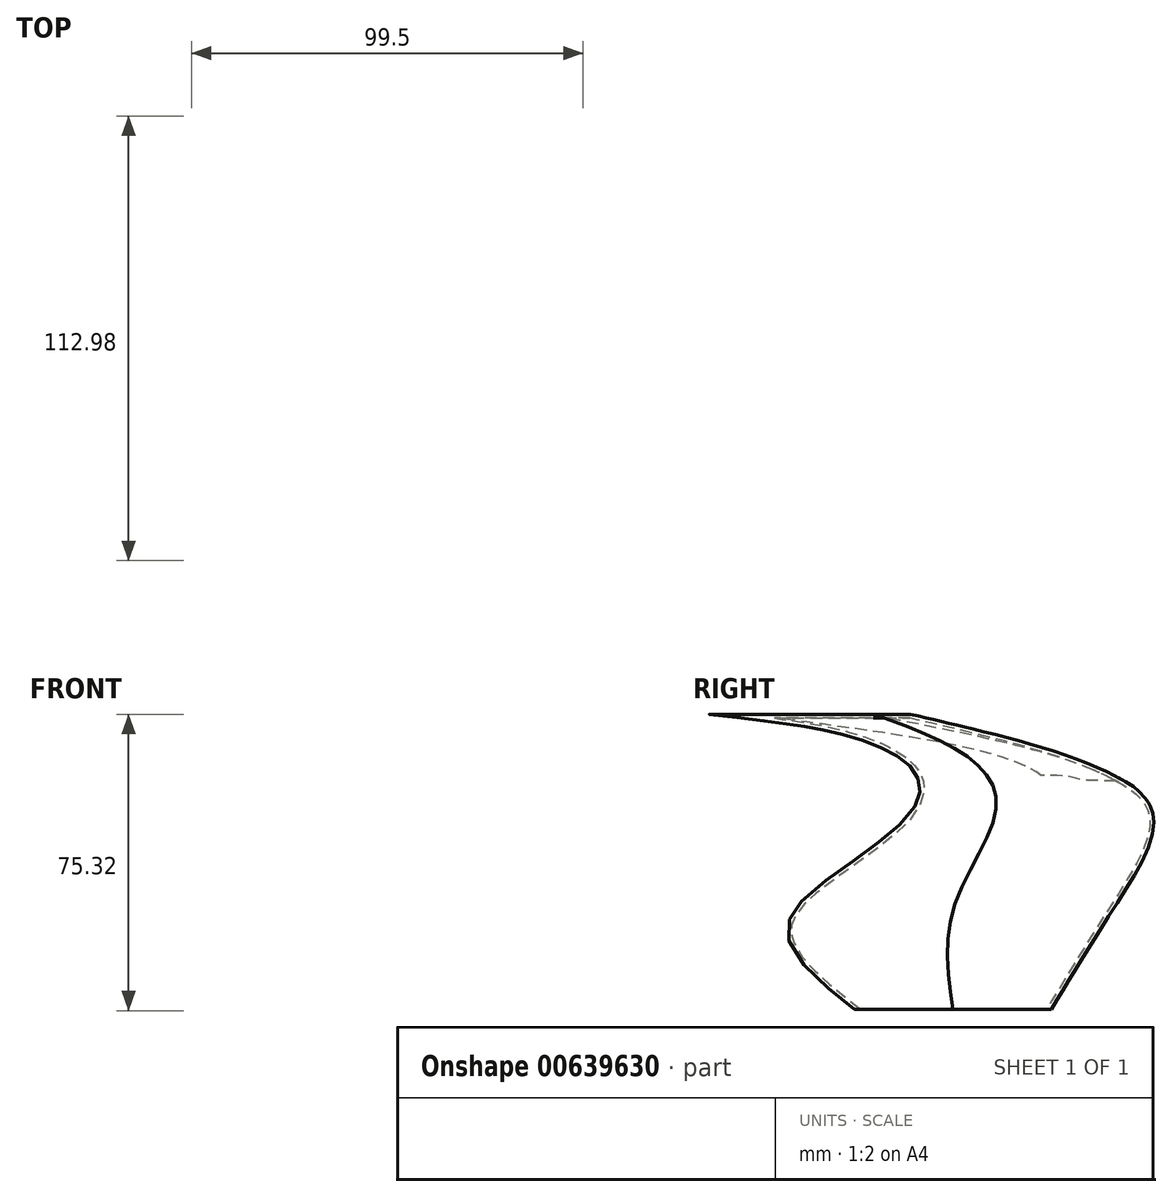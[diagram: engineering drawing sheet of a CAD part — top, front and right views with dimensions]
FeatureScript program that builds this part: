
annotation { "Feature Type Name" : "Feature", "Feature Type Description" : "" }
export const myFeature = defineFeature(function(context is Context, id is Id, definition is map)
    precondition{}
    {
        {
            var Q0;
            Q0=qCreatedBy(makeId("Top.planeOp"),FACE);
            var sketch = newSketch(context, id + "F0", { "sketchPlane" : qUnion([Q0])});
            skCircle(sketch, "E0", {"center": v(0, 0) * mm, "radius": 25 * mm});
            skSolve(sketch);
        }
        {
            var Q0;
            Q0=qCreatedBy(makeId("Top.planeOp"),FACE);
            cPlane(context, id + "F1", {"entities" : qUnion([Q0]), "cplaneType" : CPlaneType.OFFSET, "offset" : 25 * mm, "width" : 150 * mm, "height" : 150 * mm});
        }
        {
            var Q0;
            Q0=qCreatedBy(id+"F1.planeOp",FACE);
            cPlane(context, id + "F2", {"entities" : qUnion([Q0]), "cplaneType" : CPlaneType.OFFSET, "offset" : 25 * mm, "width" : 150 * mm, "height" : 150 * mm});
        }
        {
            var Q0;
            Q0=qCreatedBy(id+"F2.planeOp",FACE);
            cPlane(context, id + "F3", {"entities" : qUnion([Q0]), "cplaneType" : CPlaneType.OFFSET, "offset" : 25 * mm, "width" : 150 * mm, "height" : 150 * mm});
        }
        {
            var Q0;
            Q0=qCreatedBy(id+"F1.planeOp",FACE);
            var sketch = newSketch(context, id + "F4", { "sketchPlane" : qUnion([Q0])});
            skCircle(sketch, "E1", {"center": v(0, 0) * mm, "radius": 40.45 * mm});
            skSolve(sketch);
        }
        {
            var Q0;
            Q0=qCreatedBy(id+"F2.planeOp",FACE);
            var sketch = newSketch(context, id + "F5", { "sketchPlane" : qUnion([Q0])});
            skFitSpline(sketch, "E2", {"points": [v(-53.83, 35.8) * mm, v(-45.08, 46.36) * mm, v(-22.5, 50.73) * mm, v(21.95, 40.9) * mm, v(16.85, 6.65) * mm, v(-9.02, -10.47) * mm, v(-51.28, 22.31) * mm, v(-53.83, 35.8) * mm]});
            skSolve(sketch);
        }
        {
            var Q0;
            Q0=qCreatedBy(id+"F3.planeOp",FACE);
            var sketch = newSketch(context, id + "F6", { "sketchPlane" : qUnion([Q0])});
            skFitSpline(sketch, "E3", {"points": [v(-55.83, -51.28) * mm, v(-16.85, -57.47) * mm, v(-12.84, -23.22) * mm, v(-45.63, -13.39) * mm, v(-55.83, -51.28) * mm]});
            skSolve(sketch);
        }
        {
            var Q0;
            Q0=makeQuery(id+"F0.imprint","IMPRINT",FACE,{"disambiguationData":[TD([[makeQuery(id+"F0.imprint","IMPRINT",EDGE,{"derivedFrom":sQuery(id+"F0.wireOp",EDGE,"E0")}),1.0]])]});
            var Q1;
            Q1=makeQuery(id+"F4.imprint","IMPRINT",FACE,{"disambiguationData":[TD([[makeQuery(id+"F4.imprint","IMPRINT",EDGE,{"derivedFrom":sQuery(id+"F4.wireOp",EDGE,"E1")}),1.0]])]});
            var Q2;
            Q2=makeQuery(id+"F5.imprint","IMPRINT",FACE,{"disambiguationData":[TD([[makeQuery(id+"F5.imprint","IMPRINT",EDGE,{"derivedFrom":sQuery(id+"F5.wireOp",EDGE,"E2")}),-1.0]])]});
            var Q3;
            Q3=makeQuery(id+"F6.imprint","IMPRINT",FACE,{"disambiguationData":[TD([[makeQuery(id+"F6.imprint","IMPRINT",EDGE,{"derivedFrom":sQuery(id+"F6.wireOp",EDGE,"E3")}),1.0]])]});
            loft(context, id + "F7", {"sheetProfilesArray" : [{ "sheetProfileEntities" : qUnion([Q0]) }, { "sheetProfileEntities" : qUnion([Q1]) }, { "sheetProfileEntities" : qUnion([Q2]) }, { "sheetProfileEntities" : qUnion([Q3]) }]});
        }
        {
            var Q0;
            Q0=makeQuery(id+"F7.opLoft","CAP_FACE",FACE,{"disambiguationData":[OSD([makeQuery(id+"F0.imprint","IMPRINT",FACE,{"disambiguationData":[TD([[makeQuery(id+"F0.imprint","IMPRINT",EDGE,{"derivedFrom":sQuery(id+"F0.wireOp",EDGE,"E0")}),1.0]])]})])],"isStart":true});
            shell(context, id + "F8", {"entities" : qUnion([Q0]), "thickness" : 1 * mm});
        }
    });
